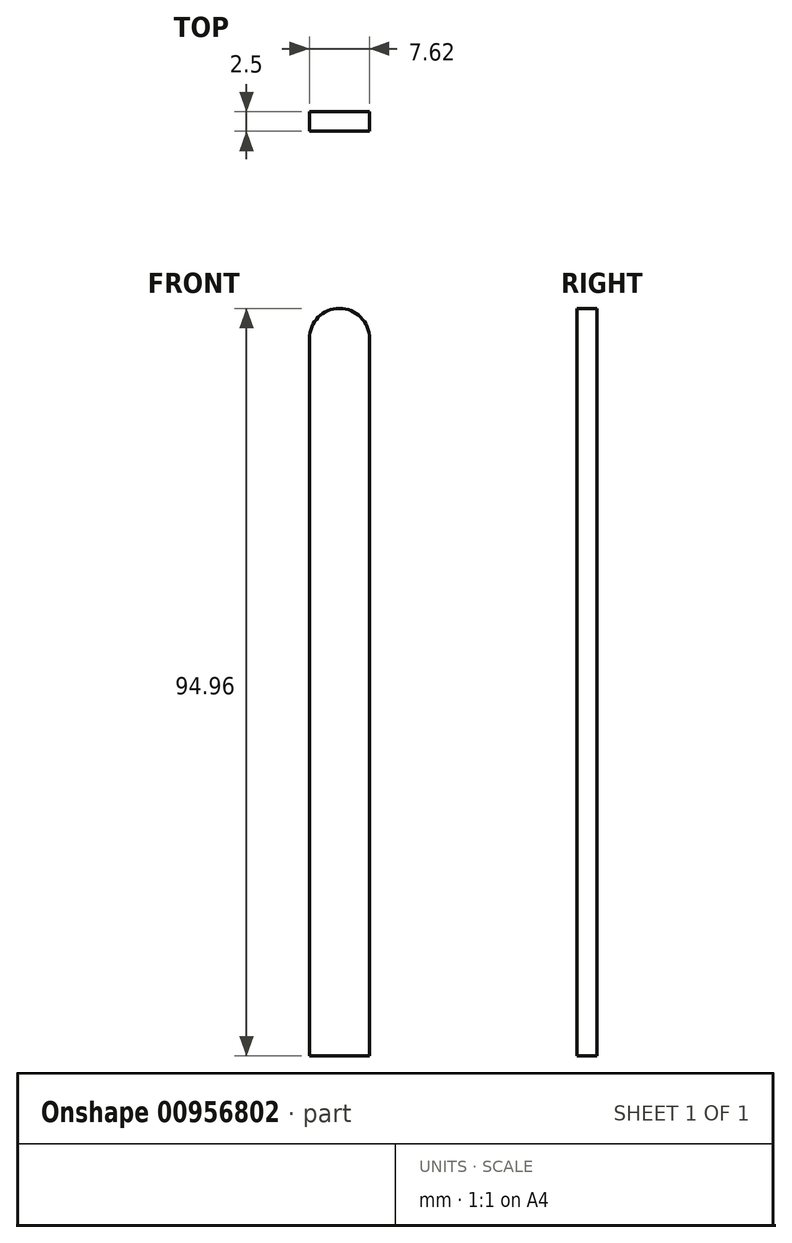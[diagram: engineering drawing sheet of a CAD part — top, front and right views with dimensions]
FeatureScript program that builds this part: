
annotation { "Feature Type Name" : "Feature", "Feature Type Description" : "" }
export const myFeature = defineFeature(function(context is Context, id is Id, definition is map)
    precondition{}
    {
        {
            var Q0;
            Q0=qCreatedBy(makeId("Front.planeOp"),FACE);
            var sketch = newSketch(context, id + "F0", { "sketchPlane" : qUnion([Q0])});
            skLineSegment(sketch, "E0.bottom", {"start": v(-39.06, 51.83) * mm, "end": v(-31.44, 51.83) * mm});
            skLineSegment(sketch, "E0.top", {"start": v(-39.06, -39.32) * mm, "end": v(-31.44, -39.32) * mm});
            skLineSegment(sketch, "E0.left", {"start": v(-39.06, 51.83) * mm, "end": v(-39.06, -39.32) * mm});
            skLineSegment(sketch, "E0.right", {"start": v(-31.44, 51.83) * mm, "end": v(-31.44, -39.32) * mm});
            skArc(sketch, "E1", {"start": v(-31.44, 51.83) * mm, "mid": v(-35.25, 55.64) * mm, "end": v(-39.06, 51.83) * mm});
            skSolve(sketch);
        }
        {
            var Q0;
            Q0=makeQuery(id+"F0.imprint","IMPRINT",FACE,{"disambiguationData":[TD([[makeQuery(id+"F0.imprint","IMPRINT",EDGE,{"derivedFrom":sQuery(id+"F0.wireOp",EDGE,"E0.bottom")}),-1.0]])]});
            var Q1;
            Q1=makeQuery(id+"F0.imprint","IMPRINT",FACE,{"disambiguationData":[TD([[makeQuery(id+"F0.imprint","IMPRINT",EDGE,{"derivedFrom":sQuery(id+"F0.wireOp",EDGE,"E0.bottom")}),1.0]])]});
            extrude(context, id + "F1", {"entities" : qUnion([Q0, Q1]), "depth" : 2.5 * mm, "offsetDistance" : 25 * mm});
        }
    });
